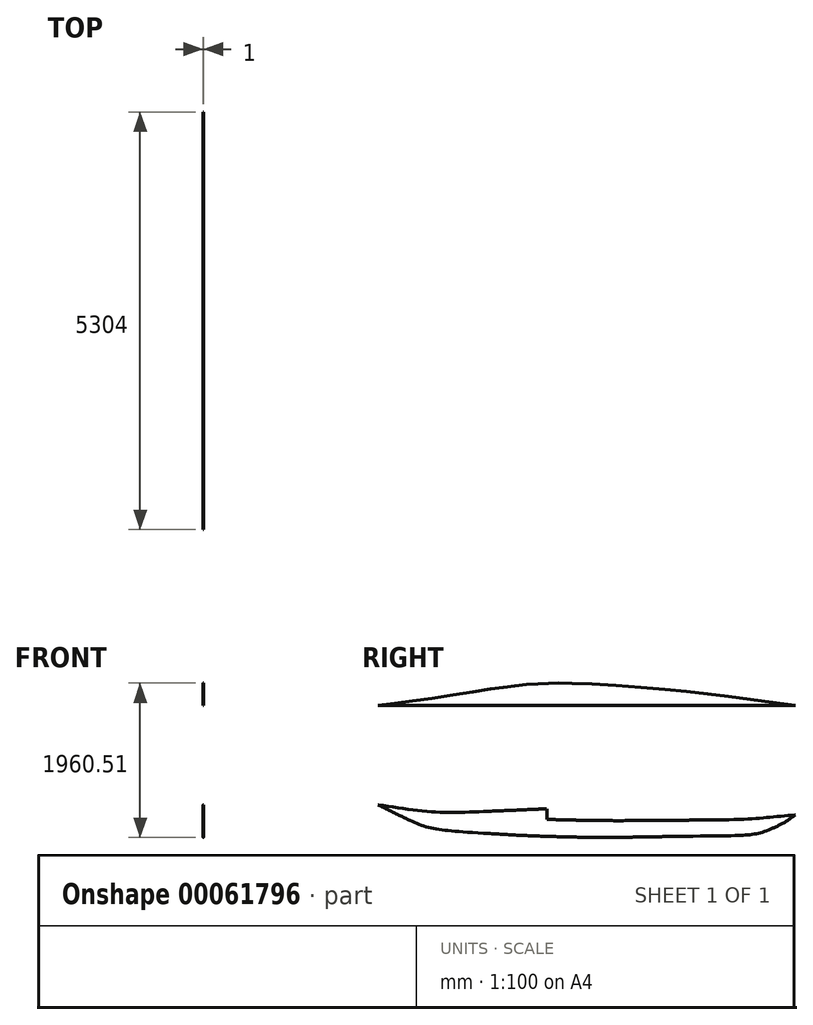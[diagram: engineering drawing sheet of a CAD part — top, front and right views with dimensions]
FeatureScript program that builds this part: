
annotation { "Feature Type Name" : "Feature", "Feature Type Description" : "" }
export const myFeature = defineFeature(function(context is Context, id is Id, definition is map)
    precondition{}
    {
        {
            var Q0;
            Q0=qCreatedBy(makeId("Right.planeOp"),FACE);
            cPlane(context, id + "F0", {"entities" : qUnion([Q0]), "cplaneType" : CPlaneType.OFFSET, "offset" : 150 * mm, "width" : 150 * mm, "height" : 150 * mm});
        }
        {
            var Q0;
            Q0=qCreatedBy(id+"F0.planeOp",FACE);
            var sketch = newSketch(context, id + "F1", { "sketchPlane" : qUnion([Q0])});
            skLineSegment(sketch, "E0", {"start": v(-2618.21, 682.38) * mm, "end": v(2685.79, 682.38) * mm});
            skLineSegment(sketch, "E1", {"start": v(-2618.21, 682.38) * mm, "end": v(-2618.21, -576.3) * mm, "construction": true});
            skLineSegment(sketch, "E2", {"start": v(2685.79, 682.38) * mm, "end": v(2685.79, -706.33) * mm, "construction": true});
            skFitSpline(sketch, "E3", {"points": [v(-2618.21, -576.3) * mm, v(-2376.84, -619.76) * mm, v(-2100.14, -666.9) * mm, v(-1791.52, -704.9) * mm, v(-1309.58, -735.3) * mm, v(-258.82, -768.8) * mm, v(411.65, -778.88) * mm, v(1276.92, -772.84) * mm, v(2043.49, -761.04) * mm, v(2372.84, -735.26) * mm, v(2685.79, -706.33) * mm], "startDerivative": vector(3387.63, -610.36) * mm, "endDerivative": vector(4024.4, 364.83) * mm});
            skFitSpline(sketch, "E4", {"points": [v(-2618.21, -576.3) * mm, v(-2425.02, -671.98) * mm, v(-2229.86, -768.12) * mm, v(-2117.93, -818.34) * mm, v(-2018.92, -854.22) * mm, v(-1901.25, -881.48) * mm, v(-1744.84, -903) * mm, v(-1487.97, -924.53) * mm, v(-899.2, -960.5) * mm, v(-389.14, -981.24) * mm, v(265.6, -992.45) * mm, v(814.04, -984.78) * mm, v(1826.63, -970.2) * mm, v(2034.84, -962.99) * mm, v(2134.7, -953.32) * mm, v(2231.35, -937.22) * mm, v(2313.5, -908.22) * mm, v(2499.52, -826.47) * mm, v(2685.79, -706.33) * mm], "startDerivative": vector(3751.82, -1853.52) * mm, "endDerivative": vector(3480.86, 2477.34) * mm});
            skFitSpline(sketch, "E5", {"points": [v(-2618.21, -576.3) * mm, v(-1921.1, -666.9) * mm, v(-1378.67, -666.9) * mm, v(-469.8, -628) * mm], "startDerivative": vector(2203.27, -343.55) * mm, "endDerivative": vector(2589, 114.68) * mm});
            skLineSegment(sketch, "E6", {"start": v(-2213.5, -775.88) * mm, "end": v(-1847.05, -827.76) * mm});
            skLineSegment(sketch, "E7", {"start": v(-1847.05, -827.76) * mm, "end": v(-1437.75, -867.88) * mm});
            skLineSegment(sketch, "E8", {"start": v(-1437.75, -867.88) * mm, "end": v(-917.25, -906.6) * mm});
            skLineSegment(sketch, "E9", {"start": v(-917.25, -906.6) * mm, "end": v(-39.96, -941.88) * mm});
            skLineSegment(sketch, "E10", {"start": v(-39.96, -941.88) * mm, "end": v(582.48, -941.88) * mm});
            skLineSegment(sketch, "E11", {"start": v(582.48, -941.88) * mm, "end": v(1606.01, -919.64) * mm});
            skLineSegment(sketch, "E12", {"start": v(1606.01, -919.64) * mm, "end": v(2063.34, -909.24) * mm});
            skLineSegment(sketch, "E13", {"start": v(2063.34, -909.24) * mm, "end": v(2385.29, -879.3) * mm});
            skLineSegment(sketch, "E14", {"start": v(585.29, -989) * mm, "end": v(585.29, -778.48) * mm});
            skFitSpline(sketch, "E15", {"points": [v(-2618.21, 682.38) * mm, v(-2009.1, 762.9) * mm, v(-1238.4, 884.04) * mm, v(-920.04, 929.52) * mm, v(-655.42, 954.33) * mm, v(-440.74, 965.05) * mm, v(-188.2, 966.73) * mm, v(817.88, 909.05) * mm, v(1732.44, 810.72) * mm, v(2685.79, 682.38) * mm], "startDerivative": vector(4913.73, 642.85) * mm, "endDerivative": vector(6767.54, -974.6) * mm});
            skLineSegment(sketch, "E16", {"start": v(-469.8, -628) * mm, "end": v(-469.8, -763.28) * mm});
            skLineSegment(sketch, "E17", {"start": v(930.29, -775.85) * mm, "end": v(930.29, -982.92) * mm});
            skLineSegment(sketch, "E18", {"start": v(635.29, -778.2) * mm, "end": v(635.29, -988.05) * mm});
            skLineSegment(sketch, "E19", {"start": v(-3157.96, -1018.5) * mm, "end": v(3327.29, -1018.5) * mm});
            skLineSegment(sketch, "E20", {"start": v(1385.29, -772.1) * mm, "end": v(1385.29, -976.67) * mm});
            skPoint(sketch, "E21.orphan", {"position": v(1385.29, -374.96) * mm});
            skPoint(sketch, "E22.orphan", {"position": v(930.29, -374.96) * mm});
            skPoint(sketch, "E23.orphan", {"position": v(930.29, -1080.55) * mm});
            skPoint(sketch, "E24.trimOffspring.end.orphan", {"position": v(1385.29, -1080.55) * mm});
            skLineSegment(sketch, "E25", {"start": v(-1274.71, -662.76) * mm, "end": v(-1274.71, -938.65) * mm});
            skLineSegment(sketch, "E26", {"start": v(-44.71, -773.73) * mm, "end": v(-44.71, -989.27) * mm});
            skLineSegment(sketch, "E27", {"start": v(-669.71, -636.85) * mm, "end": v(-669.71, -971.44) * mm});
            skLineSegment(sketch, "E28", {"start": v(1385.29, -772.1) * mm, "end": v(1385.29, 1046.67) * mm, "construction": true});
            skLineSegment(sketch, "E29", {"start": v(-684.71, -637.51) * mm, "end": v(-684.71, -970.8) * mm});
            skLineSegment(sketch, "E30", {"start": v(1732.44, 810.72) * mm, "end": v(1732.44, -1919.57) * mm, "construction": true});
            skPoint(sketch, "E31", {"position": v(1385.29, 852.9) * mm});
            skLineSegment(sketch, "E32", {"start": v(930.29, -775.85) * mm, "end": v(930.29, 899.47) * mm, "construction": true});
            skLineSegment(sketch, "E33", {"start": v(585.29, -778.48) * mm, "end": v(585.29, 926.66) * mm, "construction": true});
            skLineSegment(sketch, "E34", {"start": v(-669.71, -636.85) * mm, "end": v(-669.71, 953.32) * mm, "construction": true});
            skPoint(sketch, "E35", {"position": v(-669.71, 929.38) * mm});
            skPoint(sketch, "E36", {"position": v(585.29, 929.38) * mm});
            skPoint(sketch, "E37", {"position": v(930.29, 911.38) * mm});
            skLineSegment(sketch, "E38", {"start": v(-44.71, -773.73) * mm, "end": v(-44.71, 962.06) * mm, "construction": true});
            skPoint(sketch, "E39", {"position": v(-44.71, 957.38) * mm});
            skPoint(sketch, "E40", {"position": v(1385.29, 862.38) * mm});
            skLineSegment(sketch, "E41", {"start": v(-1274.71, -662.76) * mm, "end": v(-1274.71, 878.27) * mm, "construction": true});
            skPoint(sketch, "E42", {"position": v(-1274.71, 838.6) * mm});
            skSolve(sketch);
        }
        {
            var Q0;
            {var subQ0=sQuery(id+"F1.wireOp",EDGE,"E5");var subQ3=sQuery(id+"F1.wireOp",EDGE,"E25");var subQ5=makeQuery(id+"F1.imprint","INTERSECT",VERTEX,{"derivedFrom":[subQ0,subQ3]});Q0=makeQuery(id+"F1.imprint","IMPRINT",FACE,{"disambiguationData":[TD([[makeQuery(id+"F1.imprint","IMPRINT",EDGE,{"disambiguationData":[TD([[subQ5,-1.0]])],"derivedFrom":subQ3}),-1.0]])]});}
            var Q1;
            {var subQ0=sQuery(id+"F1.wireOp",EDGE,"E16");Q1=makeQuery(id+"F1.imprint","IMPRINT",FACE,{"disambiguationData":[TD([[makeQuery(id+"F1.imprint","IMPRINT",EDGE,{"derivedFrom":subQ0}),-1.0]])]});}
            var Q2;
            {var subQ0=sQuery(id+"F1.wireOp",EDGE,"E12");Q2=makeQuery(id+"F1.imprint","IMPRINT",FACE,{"disambiguationData":[TD([[makeQuery(id+"F1.imprint","IMPRINT",EDGE,{"derivedFrom":subQ0}),1.0]])]});}
            var Q3;
            {var subQ1=sQuery(id+"F1.wireOp",EDGE,"E6");Q3=makeQuery(id+"F1.imprint","IMPRINT",FACE,{"disambiguationData":[TD([[makeQuery(id+"F1.imprint","IMPRINT",EDGE,{"derivedFrom":subQ1}),-1.0]])]});}
            var Q4;
            {var subQ0=sQuery(id+"F1.wireOp",EDGE,"E12");Q4=makeQuery(id+"F1.imprint","IMPRINT",FACE,{"disambiguationData":[TD([[makeQuery(id+"F1.imprint","IMPRINT",EDGE,{"derivedFrom":subQ0}),-1.0]])]});}
            var Q5;
            {var subQ0=sQuery(id+"F1.wireOp",EDGE,"E6");Q5=makeQuery(id+"F1.imprint","IMPRINT",FACE,{"disambiguationData":[TD([[makeQuery(id+"F1.imprint","IMPRINT",EDGE,{"derivedFrom":subQ0}),1.0]])]});}
            var Q6;
            {var subQ0=sQuery(id+"F1.wireOp",EDGE,"E25");var subQ1=sQuery(id+"F1.wireOp",EDGE,"E3");var subQ2=makeQuery(id+"F1.imprint","INTERSECT",VERTEX,{"derivedFrom":[subQ1,subQ0]});Q6=makeQuery(id+"F1.imprint","IMPRINT",FACE,{"disambiguationData":[TD([[makeQuery(id+"F1.imprint","IMPRINT",EDGE,{"disambiguationData":[TD([[subQ2,-1.0]])],"derivedFrom":subQ1}),1.0]])]});}
            var Q7;
            {var subQ0=sQuery(id+"F1.wireOp",EDGE,"E29");var subQ1=sQuery(id+"F1.wireOp",EDGE,"E3");var subQ2=makeQuery(id+"F1.imprint","INTERSECT",VERTEX,{"derivedFrom":[subQ1,subQ0]});Q7=makeQuery(id+"F1.imprint","IMPRINT",FACE,{"disambiguationData":[TD([[makeQuery(id+"F1.imprint","IMPRINT",EDGE,{"disambiguationData":[TD([[subQ2,-1.0]])],"derivedFrom":subQ1}),1.0]])]});}
            var Q8;
            {var subQ1=sQuery(id+"F1.wireOp",EDGE,"E10");Q8=makeQuery(id+"F1.imprint","IMPRINT",FACE,{"disambiguationData":[TD([[makeQuery(id+"F1.imprint","IMPRINT",EDGE,{"derivedFrom":subQ1}),1.0]])]});}
            var Q9;
            {var subQ0=sQuery(id+"F1.wireOp",EDGE,"E14");var subQ1=sQuery(id+"F1.wireOp",EDGE,"E3");var subQ2=makeQuery(id+"F1.imprint","INTERSECT",VERTEX,{"derivedFrom":[subQ1,subQ0]});Q9=makeQuery(id+"F1.imprint","IMPRINT",FACE,{"disambiguationData":[TD([[makeQuery(id+"F1.imprint","IMPRINT",EDGE,{"disambiguationData":[TD([[subQ2,-1.0]])],"derivedFrom":subQ1}),-1.0]])]});}
            var Q10;
            {var subQ0=sQuery(id+"F1.wireOp",EDGE,"E17");var subQ1=sQuery(id+"F1.wireOp",EDGE,"E3");var subQ2=makeQuery(id+"F1.imprint","INTERSECT",VERTEX,{"derivedFrom":[subQ1,subQ0]});Q10=makeQuery(id+"F1.imprint","IMPRINT",FACE,{"disambiguationData":[TD([[makeQuery(id+"F1.imprint","IMPRINT",EDGE,{"disambiguationData":[TD([[subQ2,1.0]])],"derivedFrom":subQ1}),-1.0]])]});}
            var Q11;
            {var subQ0=sQuery(id+"F1.wireOp",EDGE,"E17");var subQ1=sQuery(id+"F1.wireOp",EDGE,"E3");var subQ2=makeQuery(id+"F1.imprint","INTERSECT",VERTEX,{"derivedFrom":[subQ1,subQ0]});Q11=makeQuery(id+"F1.imprint","IMPRINT",FACE,{"disambiguationData":[TD([[makeQuery(id+"F1.imprint","IMPRINT",EDGE,{"disambiguationData":[TD([[subQ2,-1.0]])],"derivedFrom":subQ1}),-1.0]])]});}
            var Q12;
            {var subQ0=sQuery(id+"F1.wireOp",EDGE,"E25");var subQ1=sQuery(id+"F1.wireOp",EDGE,"E4");var subQ2=makeQuery(id+"F1.imprint","INTERSECT",VERTEX,{"derivedFrom":[subQ1,subQ0]});Q12=makeQuery(id+"F1.imprint","IMPRINT",FACE,{"disambiguationData":[TD([[makeQuery(id+"F1.imprint","IMPRINT",EDGE,{"disambiguationData":[TD([[subQ2,-1.0]])],"derivedFrom":subQ1}),1.0]])]});}
            var Q13;
            {var subQ0=sQuery(id+"F1.wireOp",EDGE,"E27");var subQ1=sQuery(id+"F1.wireOp",EDGE,"E4");var subQ2=makeQuery(id+"F1.imprint","INTERSECT",VERTEX,{"derivedFrom":[subQ1,subQ0]});Q13=makeQuery(id+"F1.imprint","IMPRINT",FACE,{"disambiguationData":[TD([[makeQuery(id+"F1.imprint","IMPRINT",EDGE,{"disambiguationData":[TD([[subQ2,1.0]])],"derivedFrom":subQ1}),1.0]])]});}
            var Q14;
            {var subQ0=sQuery(id+"F1.wireOp",EDGE,"E26");var subQ1=sQuery(id+"F1.wireOp",EDGE,"E4");var subQ2=makeQuery(id+"F1.imprint","INTERSECT",VERTEX,{"derivedFrom":[subQ1,subQ0]});Q14=makeQuery(id+"F1.imprint","IMPRINT",FACE,{"disambiguationData":[TD([[makeQuery(id+"F1.imprint","IMPRINT",EDGE,{"disambiguationData":[TD([[subQ2,1.0]])],"derivedFrom":subQ1}),1.0]])]});}
            var Q15;
            {var subQ0=sQuery(id+"F1.wireOp",EDGE,"E10");Q15=makeQuery(id+"F1.imprint","IMPRINT",FACE,{"disambiguationData":[TD([[makeQuery(id+"F1.imprint","IMPRINT",EDGE,{"derivedFrom":subQ0}),-1.0]])]});}
            var Q16;
            {var subQ0=sQuery(id+"F1.wireOp",EDGE,"E14");var subQ1=sQuery(id+"F1.wireOp",EDGE,"E4");var subQ2=makeQuery(id+"F1.imprint","INTERSECT",VERTEX,{"derivedFrom":[subQ1,subQ0]});Q16=makeQuery(id+"F1.imprint","IMPRINT",FACE,{"disambiguationData":[TD([[makeQuery(id+"F1.imprint","IMPRINT",EDGE,{"disambiguationData":[TD([[subQ2,-1.0]])],"derivedFrom":subQ1}),1.0]])]});}
            var Q17;
            {var subQ0=sQuery(id+"F1.wireOp",EDGE,"E17");var subQ1=sQuery(id+"F1.wireOp",EDGE,"E4");var subQ2=makeQuery(id+"F1.imprint","INTERSECT",VERTEX,{"derivedFrom":[subQ1,subQ0]});Q17=makeQuery(id+"F1.imprint","IMPRINT",FACE,{"disambiguationData":[TD([[makeQuery(id+"F1.imprint","IMPRINT",EDGE,{"disambiguationData":[TD([[subQ2,1.0]])],"derivedFrom":subQ1}),1.0]])]});}
            var Q18;
            {var subQ0=sQuery(id+"F1.wireOp",EDGE,"E17");var subQ1=sQuery(id+"F1.wireOp",EDGE,"E4");var subQ2=makeQuery(id+"F1.imprint","INTERSECT",VERTEX,{"derivedFrom":[subQ1,subQ0]});Q18=makeQuery(id+"F1.imprint","IMPRINT",FACE,{"disambiguationData":[TD([[makeQuery(id+"F1.imprint","IMPRINT",EDGE,{"disambiguationData":[TD([[subQ2,-1.0]])],"derivedFrom":subQ1}),1.0]])]});}
            var Q19;
            {var subQ1=sQuery(id+"F1.wireOp",EDGE,"E3");var subQ7=makeQuery(id+"F1.imprint","INTERSECT",VERTEX,{"derivedFrom":[subQ1,sQuery(id+"F1.wireOp",EDGE,"E16")]});Q19=makeQuery(id+"F1.imprint","IMPRINT",FACE,{"disambiguationData":[TD([[makeQuery(id+"F1.imprint","IMPRINT",EDGE,{"disambiguationData":[TD([[subQ7,1.0]])],"derivedFrom":subQ1}),-1.0]])]});}
            var Q20;
            {var subQ5=sQuery(id+"F1.wireOp",EDGE,"E25");var subQ6=sQuery(id+"F1.wireOp",EDGE,"E3");var subQ7=makeQuery(id+"F1.imprint","INTERSECT",VERTEX,{"derivedFrom":[subQ6,subQ5]});Q20=makeQuery(id+"F1.imprint","IMPRINT",FACE,{"disambiguationData":[TD([[makeQuery(id+"F1.imprint","IMPRINT",EDGE,{"disambiguationData":[TD([[subQ7,-1.0]])],"derivedFrom":subQ6}),-1.0]])]});}
            var Q21;
            {var subQ0=sQuery(id+"F1.wireOp",EDGE,"E29");var subQ1=sQuery(id+"F1.wireOp",EDGE,"E3");var subQ2=makeQuery(id+"F1.imprint","INTERSECT",VERTEX,{"derivedFrom":[subQ1,subQ0]});Q21=makeQuery(id+"F1.imprint","IMPRINT",FACE,{"disambiguationData":[TD([[makeQuery(id+"F1.imprint","IMPRINT",EDGE,{"disambiguationData":[TD([[subQ2,-1.0]])],"derivedFrom":subQ1}),-1.0]])]});}
            var Q22;
            {var subQ0=sQuery(id+"F1.wireOp",EDGE,"E15");var subQ1=sQuery(id+"F1.wireOp",EDGE,"E0");var subQ2=makeQuery(id+"F1.imprint","INTERSECT",VERTEX,{"disambiguationData":[OD(0.0)],"derivedFrom":[subQ1,subQ0]});Q22=makeQuery(id+"F1.imprint","IMPRINT",FACE,{"disambiguationData":[TD([[makeQuery(id+"F1.imprint","IMPRINT",EDGE,{"disambiguationData":[TD([[subQ2,-1.0]])],"derivedFrom":subQ1}),1.0]])]});}
            var Q23;
            {var subQ0=sQuery(id+"F1.wireOp",EDGE,"E15");var subQ1=sQuery(id+"F1.wireOp",EDGE,"E0");var subQ2=makeQuery(id+"F1.imprint","INTERSECT",VERTEX,{"disambiguationData":[OD(1.0)],"derivedFrom":[subQ1,subQ0]});Q23=makeQuery(id+"F1.imprint","IMPRINT",FACE,{"disambiguationData":[TD([[makeQuery(id+"F1.imprint","IMPRINT",EDGE,{"disambiguationData":[TD([[subQ2,1.0]])],"derivedFrom":subQ1}),1.0]])]});}
            extrude(context, id + "F2", {"entities" : qUnion([Q0, Q1, Q2, Q3, Q4, Q5, Q6, Q7, Q8, Q9, Q10, Q11, Q12, Q13, Q14, Q15, Q16, Q17, Q18, Q19, Q20, Q21, Q22, Q23]), "endBound" : BoundingType.SYMMETRIC, "depth" : 1 * mm});
        }
    });
